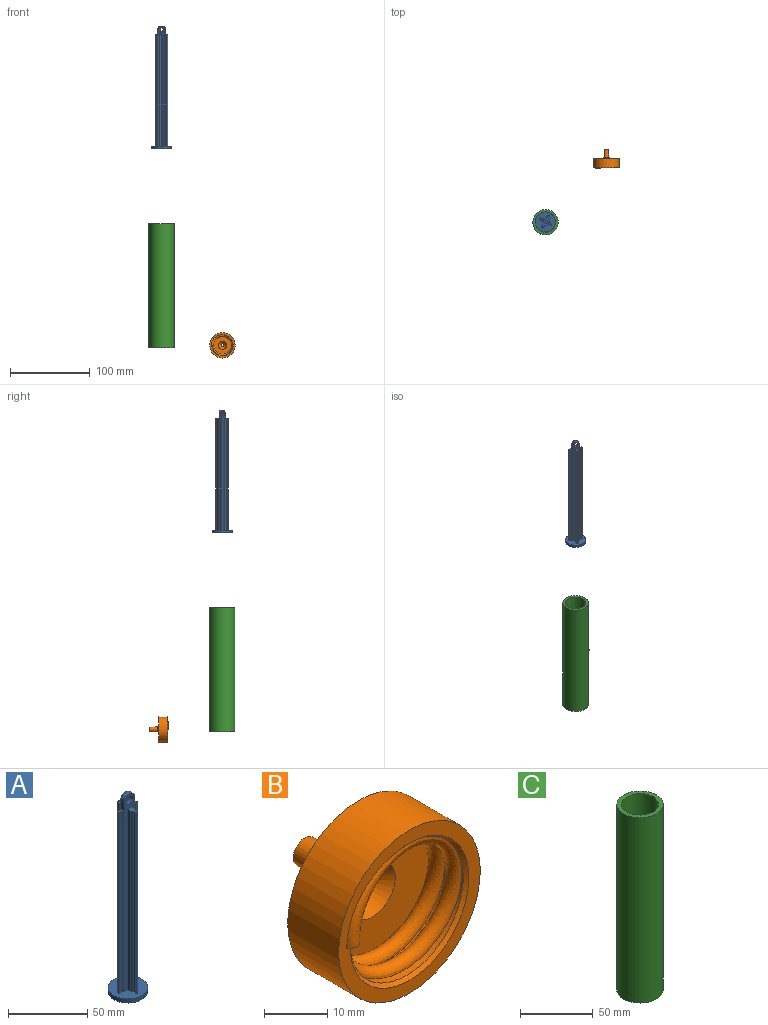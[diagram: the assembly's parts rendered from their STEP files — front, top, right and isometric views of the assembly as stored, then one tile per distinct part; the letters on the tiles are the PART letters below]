
ASSEMBLY  parts=3 mates=1
PART A: 37 faces, bbox 25.1x25.1x153.8 mm
  f0: plane 7.05x3.73mm, normal (0,0,1), area 19.9mm2, adj f16,f17,f18,f19,f20,f21,f22,f23
  f1: plane 4.18x3.54mm, normal (0,0,1), area 8.6mm2, adj f11,f12,f13,f14,f15,f34
  f2: plane 7.05x3.73mm, normal (0,0,1), area 19.9mm2, adj f6,f7,f8,f9,f10,f29,f30,f31
  f3: cylinder r=12.57mm len=25.15mm, axis (0,0,-1), area 250.8mm2, adj f4,f5
  f4: plane 25.15x25.15mm, normal (0,0,1), area 407.5mm2, adj f3,f6,f7,f8,f9,f10,f11,f12
  f5: plane 25.15x25.15mm, normal (0,0,-1), area 496.6mm2, adj f3
  f6: cylinder r=0.89mm len=139.7mm, axis (0,0,-1), area 389.5mm2, adj f2,f4,f7,f31
  f7: plane 139.7x1.75mm, normal (-1,0,0), area 244.5mm2, adj f2,f4,f6,f8
  f8: cylinder r=1.86mm len=139.7mm, axis (0,0,-1), area 279.7mm2, adj f2,f4,f7,f9
  f9: plane 139.7x2.78mm, normal (-1,0,0), area 388mm2, adj f2,f4,f8,f10
  f10: plane 150.6x9.1mm, normal (0,1,0), area 808.7mm2, adj f2,f4,f9,f11,f28,f29,f33,f34
  f11: cylinder r=1.77mm len=139.7mm, axis (0,0,-1), area 273.5mm2, adj f1,f4,f10,f12
  f12: plane 139.7x1.81mm, normal (0,1,0), area 252.4mm2, adj f1,f4,f11,f13
  f13: cylinder r=0.79mm len=139.7mm, axis (0,0,-1), area 348.4mm2, adj f1,f4,f12,f14
  f14: plane 139.7x1.81mm, normal (0,-1,0), area 252.4mm2, adj f1,f4,f13,f15
  f15: cylinder r=1.77mm len=139.7mm, axis (0,0,-1), area 273.5mm2, adj f1,f4,f14,f16
  f16: plane 150.6x9.1mm, normal (0,-1,0), area 808.7mm2, adj f0,f4,f15,f17,f23,f24,f33,f34
  f17: plane 139.7x2.78mm, normal (-1,0,0), area 388mm2, adj f0,f4,f16,f18
  f18: cylinder r=1.86mm len=139.7mm, axis (0,0,-1), area 279.7mm2, adj f0,f4,f17,f19
  f19: plane 139.7x1.75mm, normal (-1,0,0), area 244.5mm2, adj f0,f4,f18,f20
  f20: cylinder r=0.89mm len=139.7mm, axis (0,0,-1), area 389.5mm2, adj f0,f4,f19,f21
  f21: plane 139.7x1.75mm, normal (1,0,0), area 244.5mm2, adj f0,f4,f20,f22
  f22: cylinder r=1.86mm len=139.7mm, axis (0,0,-1), area 279.7mm2, adj f0,f4,f21,f23
  f23: plane 139.7x2.78mm, normal (1,0,0), area 388mm2, adj f0,f4,f16,f22
  f24: cylinder r=1.77mm len=139.7mm, axis (0,0,-1), area 273.5mm2, adj f4,f16,f25,f32
  f25: plane 139.7x1.81mm, normal (0,-1,0), area 252.4mm2, adj f4,f24,f26,f32
  f26: cylinder r=0.79mm len=139.7mm, axis (0,0,-1), area 348.4mm2, adj f4,f25,f27,f32
  f27: plane 139.7x1.81mm, normal (0,1,0), area 252.4mm2, adj f4,f26,f28,f32
  f28: cylinder r=1.77mm len=139.7mm, axis (0,0,-1), area 273.5mm2, adj f4,f10,f27,f32
  f29: plane 139.7x2.78mm, normal (1,0,0), area 388mm2, adj f2,f4,f10,f30
  f30: cylinder r=1.86mm len=139.7mm, axis (0,0,-1), area 279.7mm2, adj f2,f4,f29,f31
  f31: plane 139.7x1.75mm, normal (1,0,0), area 244.5mm2, adj f2,f4,f6,f30
  f32: plane 4.18x3.54mm, normal (0,0,1), area 8.6mm2, adj f24,f25,f26,f27,f28,f33
  f33: plane 6.35x3.54mm, normal (1,0,0), area 22.5mm2, adj f10,f16,f32,f35
  f34: plane 6.35x3.54mm, normal (-1,0,0), area 22.5mm2, adj f1,f10,f16,f35
  f35: cylinder r=4.55mm len=9.1mm, axis (0,1,0), area 50.6mm2, adj f10,f16,f33,f34
  f36: cylinder r=3.17mm len=6.35mm, axis (0,-1,0), area 70.6mm2, adj f10,f16
PART B: 13 faces, bbox 32.8x25.5x32.8 mm
  f0: plane 32.19x32.19mm, normal (0,-1,0), area 225.2mm2, adj f2,f3,f10,f12
  f1: cylinder r=12.7mm len=25.4mm, axis (0,1,0), area 170.3mm2, adj f2,f9,f10,f11,f12
  f2: cone r=1.91mm half-angle=45deg, axis (0,-1,0), area 51.5mm2, adj f0,f1,f10,f12
  f3: cylinder r=15.88mm len=31.75mm, axis (0,1,0), area 1140.1mm2, adj f0,f4
  f4: plane 31.75x31.75mm, normal (0,1,0), area 722.9mm2, adj f3,f7
  f5: cone r=3.17mm half-angle=3deg, axis (0,-1,0), area 188.2mm2, adj f6,f7
  f6: cone r=1.91mm half-angle=3deg, axis (0,1,0), area 169.4mm2, adj f5,f8
  f7: torus R=4.68mm, axis (0,-1,0), area 55.9mm2, adj f4,f5
  f8: cone r=1.91mm half-angle=45deg, axis (0,-1,0), area 98.5mm2, adj f6,f9
  f9: plane 26.42x25.25mm, normal (0,-1,0), area 389.3mm2, adj f1,f8,f11,f12
  f10: plane 3.71x3.57mm, normal (0,0,-1), area 4.7mm2, adj f0,f1,f2,f12
  f11: plane 1.96x1.96mm, normal (0,0,1), area 1.8mm2, adj f1,f9,f12
  f12: bspline ~28.16x28.14mm, area 691.6mm2, adj f0,f1,f2,f9,f10,f11
PART C: 7 faces, bbox 31.8x31.8x155.6 mm
  f0: cylinder r=12.7mm len=152.4mm, axis (0,0,-1), area 12161mm2, adj f2,f3
  f1: cylinder r=15.88mm len=155.58mm, axis (0,0,-1), area 15517.9mm2, adj f2,f4
  f2: plane 31.75x31.75mm, normal (0,0,1), area 285mm2, adj f0,f1
  f3: plane 25.4x25.4mm, normal (0,0,1), area 471.1mm2, adj f0,f5,f6
  f4: plane 31.75x31.75mm, normal (0,0,-1), area 756.1mm2, adj f1,f5,f6
  f5: cylinder r=2.38mm len=4.76mm, axis (0,0,-1), area 47.5mm2, adj f3,f4
  f6: cylinder r=2.38mm len=4.76mm, axis (0,0,-1), area 47.5mm2, adj f3,f4
PLACE A rot(axis=(0,0,-1),27.9deg) t=(-154.1,36.19,221.14)mm
PLACE B t=(-50.51,32.84,-25.25)mm
PLACE C t=(-50.51,32.84,-25.25)mm fixed
MATE cylindrical A.f3 <-> C.f0  axis (0,0,-1) through (-126.91,-43.76,224.32)mm
